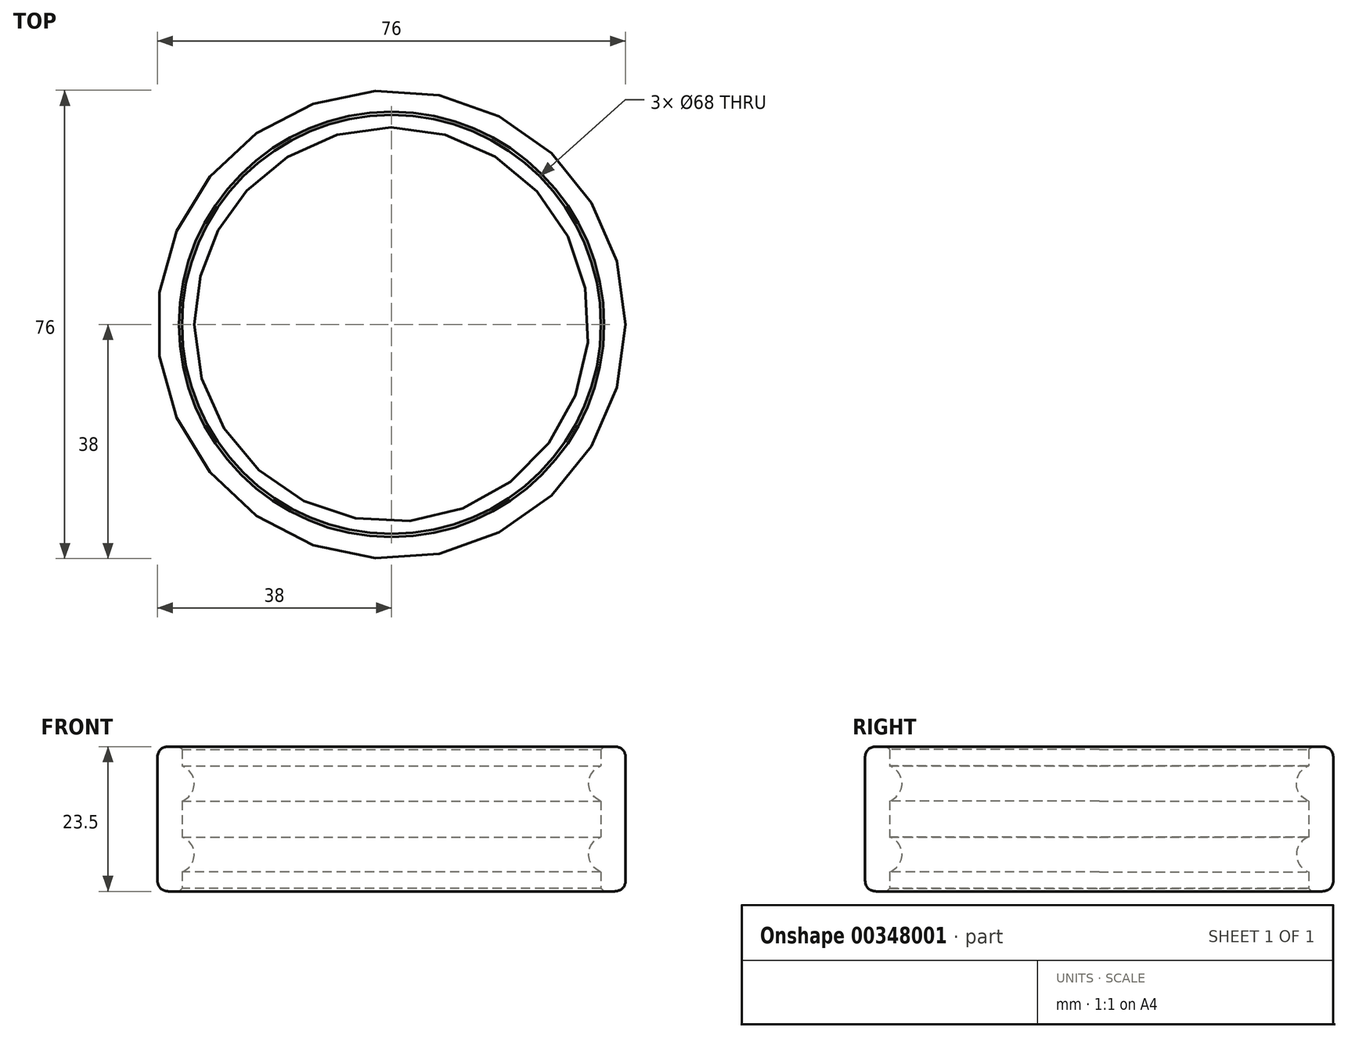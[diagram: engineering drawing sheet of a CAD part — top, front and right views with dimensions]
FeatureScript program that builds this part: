
annotation { "Feature Type Name" : "Feature", "Feature Type Description" : "" }
export const myFeature = defineFeature(function(context is Context, id is Id, definition is map)
    precondition{}
    {
        {
            var Q0;
            Q0=qCreatedBy(makeId("Top.planeOp"),FACE);
            var sketch = newSketch(context, id + "F0", { "sketchPlane" : qUnion([Q0])});
            skCircle(sketch, "E0", {"center": v(0, 0) * mm, "radius": 34 * mm});
            skCircle(sketch, "E1", {"center": v(0, 0) * mm, "radius": 38 * mm});
            skSolve(sketch);
        }
        {
            var Q0;
            Q0=makeQuery(id+"F0.imprint","IMPRINT",FACE,{"disambiguationData":[TD([[makeQuery(id+"F0.imprint","IMPRINT",EDGE,{"derivedFrom":sQuery(id+"F0.wireOp",EDGE,"E0")}),-1.0]])]});
            extrude(context, id + "F1", {"entities" : qUnion([Q0]), "depth" : 23.5 * mm});
        }
        {
            var Q0;
            Q0=qCreatedBy(makeId("Front.planeOp"),FACE);
            var sketch = newSketch(context, id + "F2", { "sketchPlane" : qUnion([Q0])});
            skArc(sketch, "E2", {"start": v(35.83, 8.88) * mm, "mid": v(32, 6) * mm, "end": v(35.83, 3.12) * mm});
            skArc(sketch, "E3", {"start": v(35.83, 20.38) * mm, "mid": v(32, 17.5) * mm, "end": v(35.83, 14.62) * mm});
            skLineSegment(sketch, "E4", {"start": v(35.83, 20.38) * mm, "end": v(35.83, 14.62) * mm});
            skLineSegment(sketch, "E5.trimOffspring", {"start": v(35.83, 8.88) * mm, "end": v(35.83, 3.12) * mm});
            skLineSegment(sketch, "E6", {"start": v(0, 0) * mm, "end": v(0, 38.7) * mm, "construction": true});
            skSolve(sketch);
        }
        {
            var Q0;
            Q0 = qSketchRegion(id + "F2", true);
            var Q1;
            Q1=sQuery(id+"F2.wireOp",EDGE,"E6");
            revolve(context, id + "F3", {"operationType" : NewBodyOperationType.ADD, "entities" : qUnion([Q0]), "axis" : qUnion([Q1]), "revolveType" : RevolveType.FULL});
        }
        {
            var Q0;
            Q0=makeQuery(id+"F1.opExtrude","CAP_EDGE",EDGE,{"disambiguationData":[OSD([sQuery(id+"F0.wireOp",EDGE,"E1")])],"isStart":false});
            var Q1;
            Q1=makeQuery(id+"F1.opExtrude","CAP_EDGE",EDGE,{"disambiguationData":[OSD([sQuery(id+"F0.wireOp",EDGE,"E1")])],"isStart":true});
            fillet(context, id + "F4", {"entities" : qUnion([Q0, Q1]), "radius" : 2 * mm, "tangentPropagation" : true, "rho" : 0.5, "crossSection" : FilletCrossSection.CONIC, "allowEdgeOverflow" : false});
        }
        {
            var Q0;
            Q0=makeQuery(id+"F1.opExtrude","CAP_EDGE",EDGE,{"disambiguationData":[OSD([sQuery(id+"F0.wireOp",EDGE,"E0")])],"isStart":true});
            var Q1;
            Q1=makeQuery(id+"F1.opExtrude","CAP_EDGE",EDGE,{"disambiguationData":[OSD([sQuery(id+"F0.wireOp",EDGE,"E0")])],"isStart":false});
            chamfer(context, id + "F5", {"entities" : qUnion([Q0, Q1]), "width" : 0.5 * mm, "tangentPropagation" : true});
        }
    });
